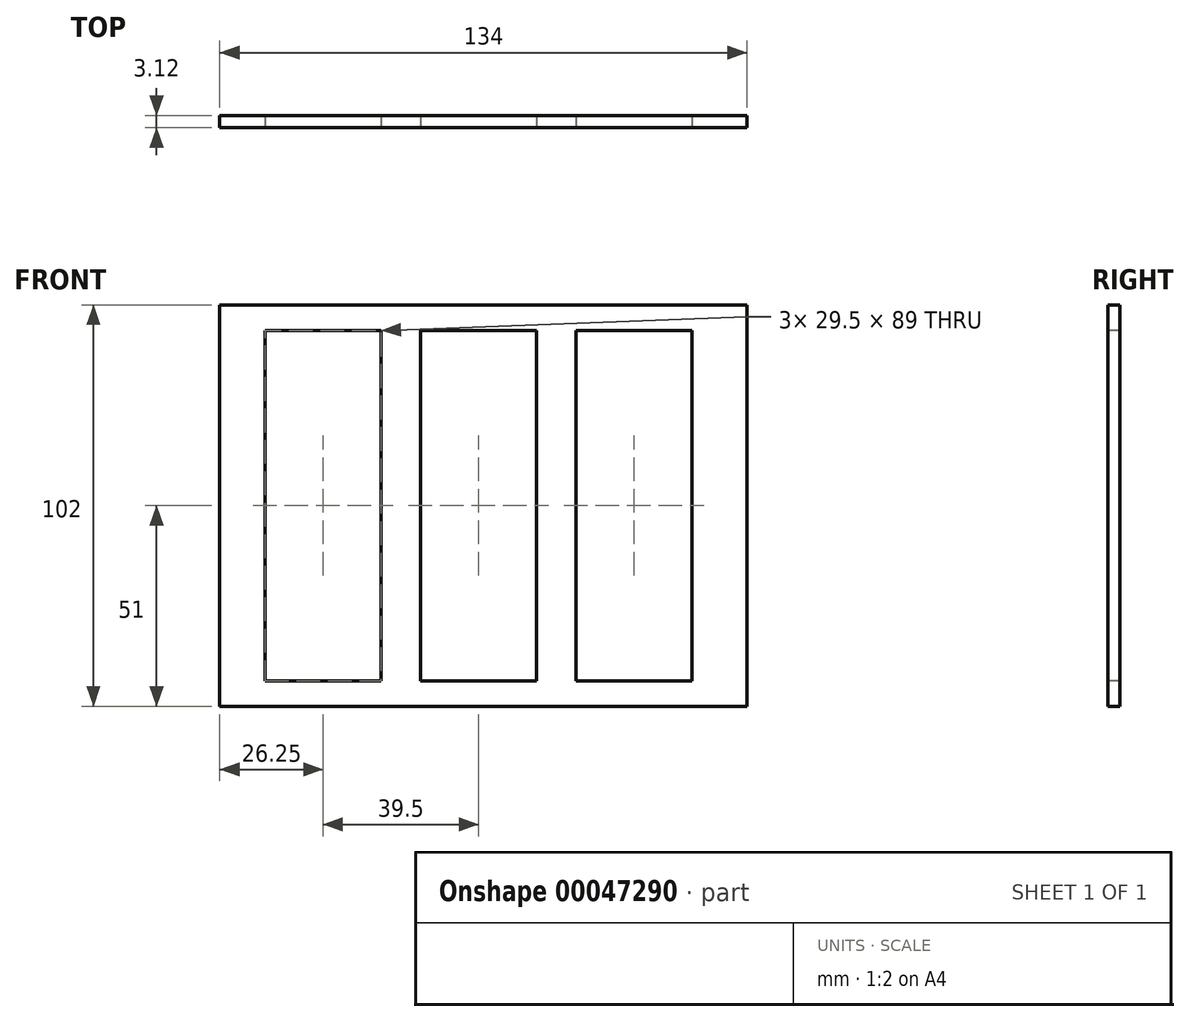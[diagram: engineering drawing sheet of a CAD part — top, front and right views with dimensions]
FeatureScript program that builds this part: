
annotation { "Feature Type Name" : "Feature", "Feature Type Description" : "" }
export const myFeature = defineFeature(function(context is Context, id is Id, definition is map)
    precondition{}
    {
        {
            var Q0;
            Q0=qCreatedBy(makeId("Front.planeOp"),FACE);
            var sketch = newSketch(context, id + "F0", { "sketchPlane" : qUnion([Q0])});
            skLineSegment(sketch, "E0.rect.bottom", {"start": v(-67, 51) * mm, "end": v(67, 51) * mm});
            skLineSegment(sketch, "E0.rect.top", {"start": v(-67, -51) * mm, "end": v(67, -51) * mm});
            skLineSegment(sketch, "E0.rect.left", {"start": v(-67, 51) * mm, "end": v(-67, -51) * mm});
            skLineSegment(sketch, "E0.rect.right", {"start": v(67, 51) * mm, "end": v(67, -51) * mm});
            skPoint(sketch, "E0.rect.middle", {"position": v(0, 0) * mm});
            skSolve(sketch);
        }
        {
            var Q0;
            Q0=qSketchRegion(id+"F0",true);
            extrude(context, id + "F1", {"entities" : qUnion([Q0]), "depth" : 3.12 * mm});
        }
        {
            var Q0;
            Q0=makeQuery(id+"F1.opExtrude","CAP_FACE",FACE,{"disambiguationData":[OSD([sQuery(id+"F0.wireOp",EDGE,"E0.rect.bottom"),sQuery(id+"F0.wireOp",EDGE,"E0.rect.top"),sQuery(id+"F0.wireOp",EDGE,"E0.rect.left"),sQuery(id+"F0.wireOp",EDGE,"E0.rect.right")])],"isStart":false});
            var sketch = newSketch(context, id + "F2", { "sketchPlane" : qUnion([Q0])});
            skLineSegment(sketch, "E1.bottom", {"start": v(-55.5, 39.8) * mm, "end": v(-26, 39.8) * mm});
            skLineSegment(sketch, "E1.top", {"start": v(-55.5, -39.8) * mm, "end": v(-26, -39.8) * mm});
            skLineSegment(sketch, "E1.left", {"start": v(-55.5, 39.8) * mm, "end": v(-55.5, -39.8) * mm});
            skLineSegment(sketch, "E1.right", {"start": v(-26, 39.8) * mm, "end": v(-26, -39.8) * mm});
            skLineSegment(sketch, "E2.bottom", {"start": v(23.5, 39.8) * mm, "end": v(53, 39.8) * mm});
            skLineSegment(sketch, "E2.top", {"start": v(23.5, -39.8) * mm, "end": v(53, -39.8) * mm});
            skLineSegment(sketch, "E2.left", {"start": v(23.5, 39.8) * mm, "end": v(23.5, -39.8) * mm});
            skLineSegment(sketch, "E2.right", {"start": v(53, 39.8) * mm, "end": v(53, -39.8) * mm});
            skLineSegment(sketch, "E3.bottom", {"start": v(-16, 39.8) * mm, "end": v(13.5, 39.8) * mm});
            skLineSegment(sketch, "E3.top", {"start": v(-16, -39.8) * mm, "end": v(13.5, -39.8) * mm});
            skLineSegment(sketch, "E3.left", {"start": v(-16, 39.8) * mm, "end": v(-16, -39.8) * mm});
            skLineSegment(sketch, "E3.right", {"start": v(13.5, 39.8) * mm, "end": v(13.5, -39.8) * mm});
            skSolve(sketch);
        }
        {
            var Q0;
            Q0=qSketchRegion(id+"F2",true);
            extrude(context, id + "F3", {"entities" : qUnion([Q0]), "operationType" : NewBodyOperationType.REMOVE, "oppositeDirection" : true, "depth" : 3.17 * mm});
        }
        {
            var Q0;
            Q0=makeQuery(id+"F1.opExtrude","CAP_FACE",FACE,{"disambiguationData":[OSD([sQuery(id+"F0.wireOp",EDGE,"E0.rect.bottom"),sQuery(id+"F0.wireOp",EDGE,"E0.rect.top"),sQuery(id+"F0.wireOp",EDGE,"E0.rect.left"),sQuery(id+"F0.wireOp",EDGE,"E0.rect.right")])],"isStart":false});
            var sketch = newSketch(context, id + "F4", { "sketchPlane" : qUnion([Q0])});
            skLineSegment(sketch, "E4.bottom", {"start": v(-58.5, 44.5) * mm, "end": v(58.5, 44.5) * mm});
            skLineSegment(sketch, "E4.top", {"start": v(-58.5, 37) * mm, "end": v(58.5, 37) * mm});
            skLineSegment(sketch, "E4.left", {"start": v(-58.5, 44.5) * mm, "end": v(-58.5, 37) * mm});
            skLineSegment(sketch, "E4.right", {"start": v(58.5, 44.5) * mm, "end": v(58.5, 37) * mm});
            skLineSegment(sketch, "E5.rect.bottom", {"start": v(67, -2.63) * mm, "end": v(-67, -2.63) * mm});
            skLineSegment(sketch, "E5.rect.top", {"start": v(67, 2.62) * mm, "end": v(-67, 2.62) * mm});
            skLineSegment(sketch, "E5.rect.left", {"start": v(67, -2.63) * mm, "end": v(67, 2.62) * mm});
            skLineSegment(sketch, "E5.rect.right", {"start": v(-67, -2.63) * mm, "end": v(-67, 2.62) * mm});
            skPoint(sketch, "E5.rect.middle", {"position": v(0, 0) * mm});
            skLineSegment(sketch, "E6", {"start": v(-58.5, 37) * mm, "end": v(-67, 37) * mm, "construction": true});
            skLineSegment(sketch, "E7", {"start": v(58.5, 37) * mm, "end": v(67, 37) * mm, "construction": true});
            skLineSegment(sketch, "E8", {"start": v(-67, 0) * mm, "end": v(67, 0) * mm, "construction": true});
            skLineSegment(sketch, "E9.MirrorCS", {"start": v(-58.5, -37) * mm, "end": v(58.5, -37) * mm});
            skLineSegment(sketch, "E10.MirrorCS", {"start": v(-58.5, -44.5) * mm, "end": v(-58.5, -37) * mm});
            skLineSegment(sketch, "E11.MirrorCS", {"start": v(58.5, -44.5) * mm, "end": v(58.5, -37) * mm});
            skLineSegment(sketch, "E12.MirrorCS", {"start": v(-58.5, -44.5) * mm, "end": v(58.5, -44.5) * mm});
            skSolve(sketch);
        }
        {
            var Q0;
            Q0=makeQuery(id+"F4.imprint","IMPRINT",FACE,{"disambiguationData":[TD([[makeQuery(id+"F4.imprint","IMPRINT",EDGE,{"derivedFrom":sQuery(id+"F4.wireOp",EDGE,"E4.bottom")}),1.0]])]});
            var sketch = newSketch(context, id + "F5", { "sketchPlane" : qUnion([Q0])});
            skLineSegment(sketch, "E13.bottom", {"start": v(-55.5, 39.8) * mm, "end": v(-26, 39.8) * mm});
            skLineSegment(sketch, "E13.top", {"start": v(-55.5, 44.5) * mm, "end": v(-26, 44.5) * mm});
            skLineSegment(sketch, "E13.left", {"start": v(-55.5, 39.8) * mm, "end": v(-55.5, 44.5) * mm});
            skLineSegment(sketch, "E13.right", {"start": v(-26, 39.8) * mm, "end": v(-26, 44.5) * mm});
            skLineSegment(sketch, "E14.bottom", {"start": v(-16, 44.5) * mm, "end": v(13.5, 44.5) * mm});
            skLineSegment(sketch, "E14.top", {"start": v(-16, 39.8) * mm, "end": v(13.5, 39.8) * mm});
            skLineSegment(sketch, "E14.left", {"start": v(-16, 44.5) * mm, "end": v(-16, 39.8) * mm});
            skLineSegment(sketch, "E14.right", {"start": v(13.5, 44.5) * mm, "end": v(13.5, 39.8) * mm});
            skLineSegment(sketch, "E15.bottom", {"start": v(23.5, 44.5) * mm, "end": v(53, 44.5) * mm});
            skLineSegment(sketch, "E15.top", {"start": v(23.5, 39.8) * mm, "end": v(53, 39.8) * mm});
            skLineSegment(sketch, "E15.left", {"start": v(23.5, 44.5) * mm, "end": v(23.5, 39.8) * mm});
            skLineSegment(sketch, "E15.right", {"start": v(53, 44.5) * mm, "end": v(53, 39.8) * mm});
            skLineSegment(sketch, "E16.MirrorCS", {"start": v(23.5, -39.8) * mm, "end": v(53, -39.8) * mm});
            skLineSegment(sketch, "E17.MirrorCS", {"start": v(53, -44.5) * mm, "end": v(53, -39.8) * mm});
            skLineSegment(sketch, "E18.MirrorCS", {"start": v(23.5, -44.5) * mm, "end": v(53, -44.5) * mm});
            skLineSegment(sketch, "E19.MirrorCS", {"start": v(23.5, -44.5) * mm, "end": v(23.5, -39.8) * mm});
            skLineSegment(sketch, "E20.MirrorCS", {"start": v(13.5, -44.5) * mm, "end": v(13.5, -39.8) * mm});
            skLineSegment(sketch, "E21.MirrorCS", {"start": v(-16, -39.8) * mm, "end": v(13.5, -39.8) * mm});
            skLineSegment(sketch, "E22.MirrorCS", {"start": v(-16, -44.5) * mm, "end": v(-16, -39.8) * mm});
            skLineSegment(sketch, "E23.MirrorCS", {"start": v(-16, -44.5) * mm, "end": v(13.5, -44.5) * mm});
            skLineSegment(sketch, "E24.MirrorCS", {"start": v(-55.5, -39.8) * mm, "end": v(-26, -39.8) * mm});
            skLineSegment(sketch, "E25.MirrorCS", {"start": v(-26, -39.8) * mm, "end": v(-26, -44.5) * mm});
            skLineSegment(sketch, "E26.MirrorCS", {"start": v(-55.5, -44.5) * mm, "end": v(-26, -44.5) * mm});
            skLineSegment(sketch, "E27.MirrorCS", {"start": v(-55.5, -39.8) * mm, "end": v(-55.5, -44.5) * mm});
            skSolve(sketch);
        }
        {
            var Q0;
            Q0 = qSketchRegion(id + "F5", true);
            extrude(context, id + "F6", {"entities" : qUnion([Q0]), "operationType" : NewBodyOperationType.REMOVE, "oppositeDirection" : true, "depth" : 3.17 * mm});
        }
    });
